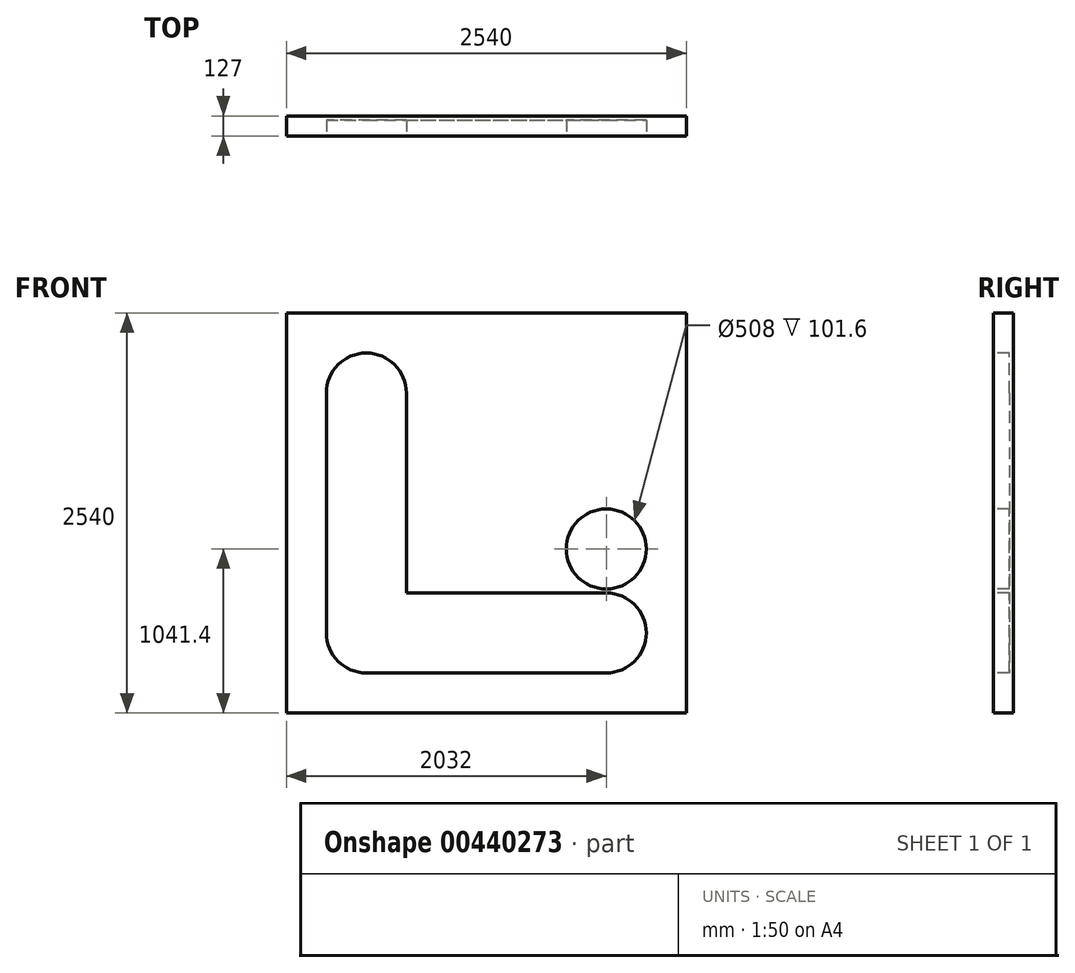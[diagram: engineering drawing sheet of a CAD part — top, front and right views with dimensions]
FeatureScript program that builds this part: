
annotation { "Feature Type Name" : "Feature", "Feature Type Description" : "" }
export const myFeature = defineFeature(function(context is Context, id is Id, definition is map)
    precondition{}
    {
        {
            var Q0;
            Q0=qCreatedBy(makeId("Front.planeOp"),FACE);
            var sketch = newSketch(context, id + "F0", { "sketchPlane" : qUnion([Q0])});
            skLineSegment(sketch, "E0.bottom", {"start": v(1270, -1270) * mm, "end": v(-1270, -1270) * mm});
            skLineSegment(sketch, "E0.top", {"start": v(1270, 1270) * mm, "end": v(-1270, 1270) * mm});
            skLineSegment(sketch, "E0.left", {"start": v(1270, -1270) * mm, "end": v(1270, 1270) * mm});
            skLineSegment(sketch, "E0.right", {"start": v(-1270, -1270) * mm, "end": v(-1270, 1270) * mm});
            skPoint(sketch, "E0.middle", {"position": v(0, 0) * mm});
            skSolve(sketch);
        }
        {
            var Q0;
            Q0 = qSketchRegion(id + "F0", true);
            extrude(context, id + "F1", {"entities" : qUnion([Q0]), "depth" : 127 * mm});
        }
        {
            var Q0;
            Q0=makeQuery(id+"F1.opExtrude","CAP_FACE",FACE,{"disambiguationData":[OSD([sQuery(id+"F0.wireOp",EDGE,"E0.bottom"),sQuery(id+"F0.wireOp",EDGE,"E0.top"),sQuery(id+"F0.wireOp",EDGE,"E0.left"),sQuery(id+"F0.wireOp",EDGE,"E0.right")])],"isStart":false});
            var sketch = newSketch(context, id + "F2", { "sketchPlane" : qUnion([Q0])});
            skLineSegment(sketch, "E1", {"start": v(-762, 762) * mm, "end": v(-762, -762) * mm, "construction": true});
            skLineSegment(sketch, "E2", {"start": v(-762, -762) * mm, "end": v(762, -762) * mm, "construction": true});
            skArc(sketch, "E3.0.startCap", {"start": v(-1016, 762) * mm, "mid": v(-762, 1016) * mm, "end": v(-508, 762) * mm});
            skArc(sketch, "E3.0.endCap", {"start": v(-508, -762) * mm, "mid": v(-762, -1016) * mm, "end": v(-1016, -762) * mm});
            skLineSegment(sketch, "E3.0.left", {"start": v(-508, 762) * mm, "end": v(-508, -762) * mm});
            skLineSegment(sketch, "E3.0.right", {"start": v(-1016, 762) * mm, "end": v(-1016, -762) * mm});
            skArc(sketch, "E3.2.startCap", {"start": v(-762, -1016) * mm, "mid": v(-1016, -762) * mm, "end": v(-762, -508) * mm});
            skArc(sketch, "E3.2.endCap", {"start": v(762, -508) * mm, "mid": v(1016, -762) * mm, "end": v(762, -1016) * mm});
            skLineSegment(sketch, "E3.2.left", {"start": v(-762, -508) * mm, "end": v(762, -508) * mm});
            skLineSegment(sketch, "E3.2.right", {"start": v(-762, -1016) * mm, "end": v(762, -1016) * mm});
            skArc(sketch, "E4.0.startCap", {"start": v(-825.5, 762) * mm, "mid": v(-762, 825.5) * mm, "end": v(-698.5, 762) * mm, "construction": true});
            skArc(sketch, "E4.0.endCap", {"start": v(-698.5, -762) * mm, "mid": v(-762, -825.5) * mm, "end": v(-825.5, -762) * mm, "construction": true});
            skLineSegment(sketch, "E4.0.left", {"start": v(-698.5, 762) * mm, "end": v(-698.5, -762) * mm, "construction": true});
            skLineSegment(sketch, "E4.0.right", {"start": v(-825.5, 762) * mm, "end": v(-825.5, -762) * mm, "construction": true});
            skArc(sketch, "E4.2.startCap", {"start": v(-762, -825.5) * mm, "mid": v(-825.5, -762) * mm, "end": v(-762, -698.5) * mm, "construction": true});
            skArc(sketch, "E4.2.endCap", {"start": v(762, -698.5) * mm, "mid": v(825.5, -762) * mm, "end": v(762, -825.5) * mm, "construction": true});
            skLineSegment(sketch, "E4.2.left", {"start": v(-762, -698.5) * mm, "end": v(762, -698.5) * mm, "construction": true});
            skLineSegment(sketch, "E4.2.right", {"start": v(-762, -825.5) * mm, "end": v(762, -825.5) * mm, "construction": true});
            skCircle(sketch, "E5", {"center": v(762, -228.6) * mm, "radius": 254 * mm});
            skSolve(sketch);
        }
        {
            var Q0;
            Q0 = qSketchRegion(id + "F2", true);
            extrude(context, id + "F3", {"entities" : qUnion([Q0]), "operationType" : NewBodyOperationType.REMOVE, "oppositeDirection" : true, "depth" : 101.6 * mm});
        }
    });
